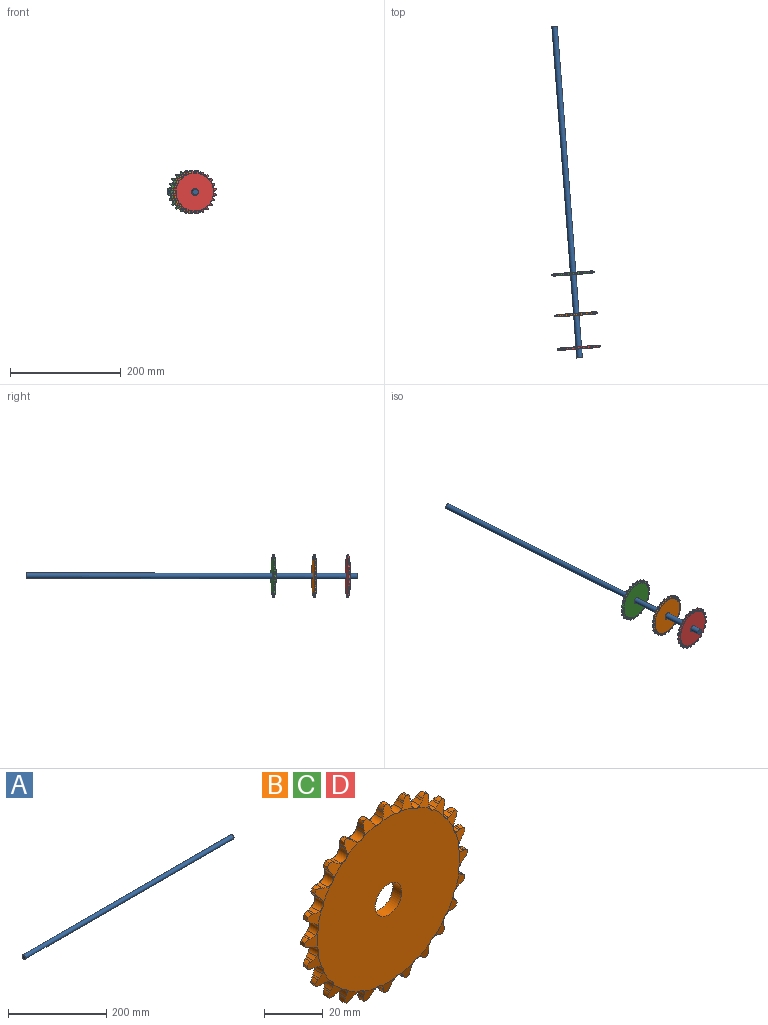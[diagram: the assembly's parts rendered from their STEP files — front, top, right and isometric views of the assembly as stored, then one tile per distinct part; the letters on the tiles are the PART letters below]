
ASSEMBLY  parts=4 mates=3
PART A: 3 faces, bbox 600x10x10 mm
  f0: cylinder r=5mm len=600mm, axis (-1,0,0), area 18849.6mm2, adj f1,f2
  f1: plane 10x10mm, normal (1,0,0), area 78.5mm2, adj f0
  f2: plane 10x10mm, normal (-1,0,0), area 78.5mm2, adj f0
PART B: 243 faces, bbox 78x4.3x78 mm
  f0: cylinder r=38.99mm len=1.91mm, axis (0,1,0), area 2.7mm2, adj f15,f45,f176,f187
  f1: cylinder r=6.35mm len=12.7mm, axis (0,1,0), area 170.3mm2, adj f16,f17
  f2: cylinder r=6.65mm len=3.92mm, axis (0,-1,0), area 6.4mm2, adj f18,f40,f208,f209
  f3: cylinder r=2.59mm len=4.27mm, axis (0,-1,0), area 19.9mm2, adj f16,f17,f20,f21,f42,f43,f196,f197
  f4: cylinder r=2.59mm len=4.27mm, axis (0,-1,0), area 19.9mm2, adj f16,f17,f21,f22,f43,f44,f190,f191
  f5: cylinder r=2.59mm len=4.27mm, axis (0,-1,0), area 19.9mm2, adj f15,f16,f17,f22,f44,f45,f184,f185
  f6: cylinder r=2.59mm len=4.27mm, axis (0,-1,0), area 19.9mm2, adj f15,f16,f17,f23,f45,f46,f178,f179
  f7: cylinder r=2.59mm len=4.27mm, axis (0,-1,0), area 19.9mm2, adj f16,f17,f23,f24,f46,f47,f172,f173
  f8: cylinder r=2.59mm len=4.27mm, axis (0,-1,0), area 19.9mm2, adj f16,f17,f24,f25,f47,f48,f166,f167
  f9: cylinder r=6.65mm len=3.92mm, axis (0,-1,0), area 6.4mm2, adj f27,f50,f154,f155
  f10: cylinder r=4.15mm len=2.78mm, axis (0,-1,0), area 4.8mm2, adj f29,f52,f131,f232
  f11: cylinder r=4.15mm len=2.78mm, axis (0,-1,0), area 4.8mm2, adj f30,f53,f125,f233
  f12: cylinder r=4.15mm len=2.78mm, axis (0,-1,0), area 4.8mm2, adj f38,f60,f82,f241
  f13: cylinder r=4.15mm len=2.78mm, axis (0,-1,0), area 4.8mm2, adj f39,f61,f76,f242
  f14: cone r=34.27mm half-angle=76deg, axis (0,-1,0), area 18.1mm2, adj f16,f97,f98,f99,f100,f107,f108,f109
  f15: cone r=39.03mm half-angle=76deg, axis (0,1,0), area 18.1mm2, adj f0,f5,f6,f17,f176,f177,f178,f185
  f16: plane 68.54x68.54mm, normal (0,1,0), area 3547.1mm2, adj f1,f3,f4,f5,f6,f7,f8,f14
  f17: plane 68.54x68.54mm, normal (0,-1,0), area 3547.1mm2, adj f1,f3,f4,f5,f6,f7,f8,f15
  f18: cone r=39.03mm half-angle=76deg, axis (0,1,0), area 18.2mm2, adj f2,f17,f207,f208,f209,f213,f214,f215
  f19: cone r=39.03mm half-angle=76deg, axis (0,1,0), area 18.1mm2, adj f17,f200,f201,f202,f203,f209,f210,f211
  f20: cone r=39.03mm half-angle=76deg, axis (0,1,0), area 18.1mm2, adj f3,f17,f194,f195,f196,f203,f204,f205
  f21: cone r=39.03mm half-angle=76deg, axis (0,1,0), area 18.1mm2, adj f3,f4,f17,f188,f189,f190,f197,f198
  f22: cone r=39.03mm half-angle=76deg, axis (0,1,0), area 18.1mm2, adj f4,f5,f17,f182,f183,f184,f191,f192
  f23: cone r=39.03mm half-angle=76deg, axis (0,1,0), area 18.1mm2, adj f6,f7,f17,f170,f171,f172,f179,f180
  f24: cone r=39.03mm half-angle=76deg, axis (0,1,0), area 18.1mm2, adj f7,f8,f17,f164,f165,f166,f173,f174
  f25: cone r=39.03mm half-angle=76deg, axis (0,1,0), area 18.1mm2, adj f8,f17,f157,f158,f159,f160,f167,f168
  f26: cone r=39.03mm half-angle=76deg, axis (0,1,0), area 18.1mm2, adj f17,f151,f152,f153,f154,f160,f161,f162
  f27: cone r=39.03mm half-angle=76deg, axis (0,1,0), area 18.2mm2, adj f9,f17,f144,f145,f146,f147,f154,f155
  f28: cone r=39.03mm half-angle=76deg, axis (0,1,0), area 18.1mm2, adj f17,f137,f138,f139,f140,f147,f148,f149
  f29: cone r=39.03mm half-angle=76deg, axis (0,1,0), area 18.2mm2, adj f10,f17,f131,f132,f133,f140,f141,f142
  f30: cone r=39.03mm half-angle=76deg, axis (0,1,0), area 18.2mm2, adj f11,f17,f125,f126,f127,f133,f134,f135
  f31: cone r=39.03mm half-angle=76deg, axis (0,1,0), area 18.1mm2, adj f17,f118,f119,f120,f121,f127,f128,f129
  f32: cone r=39.03mm half-angle=76deg, axis (0,1,0), area 18.1mm2, adj f17,f111,f112,f113,f114,f121,f122,f123
  f33: cone r=39.03mm half-angle=76deg, axis (0,1,0), area 18.1mm2, adj f17,f104,f105,f106,f107,f114,f115,f116
  f34: cone r=39.03mm half-angle=76deg, axis (0,1,0), area 18.1mm2, adj f17,f97,f98,f99,f100,f107,f108,f109
  f35: cone r=39.03mm half-angle=76deg, axis (0,1,0), area 18.1mm2, adj f17,f90,f91,f92,f93,f100,f101,f102
  f36: cone r=39.03mm half-angle=76deg, axis (0,1,0), area 18.1mm2, adj f17,f83,f84,f85,f86,f93,f94,f95
  f37: cone r=39.03mm half-angle=76deg, axis (0,1,0), area 18.1mm2, adj f17,f77,f78,f79,f80,f86,f87,f88
  f38: cone r=39.03mm half-angle=76deg, axis (0,1,0), area 18.2mm2, adj f12,f17,f71,f72,f73,f74,f80,f81
  f39: cone r=39.03mm half-angle=76deg, axis (0,1,0), area 18.2mm2, adj f13,f17,f67,f68,f69,f70,f74,f75
  f40: cone r=34.27mm half-angle=76deg, axis (0,-1,0), area 18.2mm2, adj f2,f16,f207,f208,f209,f213,f214,f215
  f41: cone r=34.27mm half-angle=76deg, axis (0,-1,0), area 18.1mm2, adj f16,f200,f201,f202,f203,f209,f210,f211
  f42: cone r=34.27mm half-angle=76deg, axis (0,-1,0), area 18.1mm2, adj f3,f16,f194,f195,f196,f203,f204,f205
  f43: cone r=34.27mm half-angle=76deg, axis (0,-1,0), area 18.1mm2, adj f3,f4,f16,f188,f189,f190,f197,f198
  f44: cone r=34.27mm half-angle=76deg, axis (0,-1,0), area 18.1mm2, adj f4,f5,f16,f182,f183,f184,f191,f192
  f45: cone r=34.27mm half-angle=76deg, axis (0,-1,0), area 18.1mm2, adj f0,f5,f6,f16,f176,f177,f178,f185
  f46: cone r=34.27mm half-angle=76deg, axis (0,-1,0), area 18.1mm2, adj f6,f7,f16,f170,f171,f172,f179,f180
  f47: cone r=34.27mm half-angle=76deg, axis (0,-1,0), area 18.1mm2, adj f7,f8,f16,f164,f165,f166,f173,f174
  f48: cone r=34.27mm half-angle=76deg, axis (0,-1,0), area 18.1mm2, adj f8,f16,f157,f158,f159,f160,f167,f168
  f49: cone r=34.27mm half-angle=76deg, axis (0,-1,0), area 18.1mm2, adj f16,f151,f152,f153,f154,f160,f161,f162
  f50: cone r=34.27mm half-angle=76deg, axis (0,-1,0), area 18.2mm2, adj f9,f16,f144,f145,f146,f147,f154,f155
  f51: cone r=34.27mm half-angle=76deg, axis (0,-1,0), area 18.1mm2, adj f16,f137,f138,f139,f140,f147,f148,f149
  f52: cone r=34.27mm half-angle=76deg, axis (0,-1,0), area 18.2mm2, adj f10,f16,f131,f132,f133,f140,f141,f142
  f53: cone r=34.27mm half-angle=76deg, axis (0,-1,0), area 18.2mm2, adj f11,f16,f125,f126,f127,f133,f134,f135
  f54: cone r=34.27mm half-angle=76deg, axis (0,-1,0), area 18.1mm2, adj f16,f118,f119,f120,f121,f127,f128,f129
  f55: cone r=34.27mm half-angle=76deg, axis (0,-1,0), area 18.1mm2, adj f16,f111,f112,f113,f114,f121,f122,f123
  f56: cone r=34.27mm half-angle=76deg, axis (0,-1,0), area 18.1mm2, adj f16,f104,f105,f106,f107,f114,f115,f116
  f57: cone r=34.27mm half-angle=76deg, axis (0,-1,0), area 18.1mm2, adj f16,f90,f91,f92,f93,f100,f101,f102
  f58: cone r=34.27mm half-angle=76deg, axis (0,-1,0), area 18.1mm2, adj f16,f83,f84,f85,f86,f93,f94,f95
  f59: cone r=34.27mm half-angle=76deg, axis (0,-1,0), area 18.1mm2, adj f16,f77,f78,f79,f80,f86,f87,f88
  f60: cone r=34.27mm half-angle=76deg, axis (0,-1,0), area 18.2mm2, adj f12,f16,f71,f72,f73,f74,f80,f81
  f61: cone r=34.27mm half-angle=76deg, axis (0,-1,0), area 18.2mm2, adj f13,f16,f67,f68,f69,f70,f74,f75
  f62: cone r=39.03mm half-angle=76deg, axis (0,1,0), area 18.1mm2, adj f17,f64,f65,f66,f67,f216,f217,f218
  f63: cone r=34.27mm half-angle=76deg, axis (0,-1,0), area 18.1mm2, adj f16,f64,f65,f66,f67,f216,f217,f218
  f64: cylinder r=4.15mm len=2.78mm, axis (0,-1,0), area 4.8mm2, adj f62,f63,f65,f220
  f65: plane 3.1x0.64mm, normal (0.97,0,-0.25), area 2mm2, adj f62,f63,f64,f66
  f66: cylinder r=6.65mm len=3.92mm, axis (0,-1,0), area 6.4mm2, adj f62,f63,f65,f67
  f67: cylinder r=2.59mm len=4.27mm, axis (0,-1,0), area 19.9mm2, adj f16,f17,f39,f61,f62,f63,f66,f68
  f68: cylinder r=6.65mm len=3.92mm, axis (0,-1,0), area 6.4mm2, adj f39,f61,f67,f69
  f69: plane 3.1x0.58mm, normal (-0.87,0,-0.49), area 2mm2, adj f39,f61,f68,f70
  f70: cylinder r=4.15mm len=2.78mm, axis (0,-1,0), area 4.8mm2, adj f39,f61,f69,f242
  f71: cylinder r=4.15mm len=2.78mm, axis (0,-1,0), area 4.8mm2, adj f38,f60,f72,f241
  f72: plane 3.1x0.48mm, normal (-0.72,0,-0.7), area 2mm2, adj f38,f60,f71,f73
  f73: cylinder r=6.65mm len=3.92mm, axis (0,-1,0), area 6.4mm2, adj f38,f60,f72,f74
  f74: cylinder r=2.59mm len=4.27mm, axis (0,-1,0), area 19.9mm2, adj f16,f17,f38,f39,f60,f61,f73,f75
  f75: cylinder r=6.65mm len=3.92mm, axis (0,-1,0), area 6.4mm2, adj f39,f61,f74,f76
  f76: plane 3.1x0.66mm, normal (1,0,0.01), area 2mm2, adj f13,f39,f61,f75
  f77: cylinder r=4.15mm len=2.78mm, axis (0,-1,0), area 4.8mm2, adj f37,f59,f78,f240
  f78: plane 3.1x0.57mm, normal (-0.51,0,-0.86), area 2mm2, adj f37,f59,f77,f79
  f79: cylinder r=6.65mm len=3.92mm, axis (0,-1,0), area 6.4mm2, adj f37,f59,f78,f80
  f80: cylinder r=2.59mm len=4.27mm, axis (0,-1,0), area 19.9mm2, adj f16,f17,f37,f38,f59,f60,f79,f81
  f81: cylinder r=6.65mm len=3.92mm, axis (0,-1,0), area 6.4mm2, adj f38,f60,f80,f82
  f82: plane 3.1x0.64mm, normal (0.96,0,0.27), area 2mm2, adj f12,f38,f60,f81
  f83: cylinder r=4.15mm len=2.78mm, axis (0,-1,0), area 4.8mm2, adj f36,f58,f84,f239
  f84: plane 3.1x0.64mm, normal (-0.27,0,-0.96), area 2mm2, adj f36,f58,f83,f85
  f85: cylinder r=6.65mm len=3.92mm, axis (0,-1,0), area 6.4mm2, adj f36,f58,f84,f86
  f86: cylinder r=2.59mm len=4.27mm, axis (0,-1,0), area 19.9mm2, adj f16,f17,f36,f37,f58,f59,f85,f87
  f87: cylinder r=6.65mm len=3.92mm, axis (0,-1,0), area 6.4mm2, adj f37,f59,f86,f88
  f88: plane 3.1x0.57mm, normal (0.86,0,0.51), area 2mm2, adj f37,f59,f87,f89
  f89: cylinder r=4.15mm len=2.78mm, axis (0,-1,0), area 4.8mm2, adj f37,f59,f88,f240
  f90: cylinder r=4.15mm len=2.78mm, axis (0,-1,0), area 4.8mm2, adj f35,f57,f91,f238
  f91: plane 3.1x0.66mm, normal (-0.01,0,-1), area 2mm2, adj f35,f57,f90,f92
  f92: cylinder r=6.65mm len=3.92mm, axis (0,-1,0), area 6.4mm2, adj f35,f57,f91,f93
  f93: cylinder r=2.59mm len=4.27mm, axis (0,-1,0), area 19.9mm2, adj f16,f17,f35,f36,f57,f58,f92,f94
  f94: cylinder r=6.65mm len=3.92mm, axis (0,-1,0), area 6.4mm2, adj f36,f58,f93,f95
  f95: plane 3.1x0.48mm, normal (0.7,0,0.72), area 2mm2, adj f36,f58,f94,f96
  f96: cylinder r=4.15mm len=2.78mm, axis (0,-1,0), area 4.8mm2, adj f36,f58,f95,f239
  f97: cylinder r=4.15mm len=2.78mm, axis (0,-1,0), area 4.8mm2, adj f14,f34,f98,f237
  f98: plane 3.1x0.64mm, normal (0.25,0,-0.97), area 2mm2, adj f14,f34,f97,f99
  f99: cylinder r=6.65mm len=3.92mm, axis (0,-1,0), area 6.4mm2, adj f14,f34,f98,f100
  f100: cylinder r=2.59mm len=4.27mm, axis (0,-1,0), area 19.9mm2, adj f14,f16,f17,f34,f35,f57,f99,f101
  f101: cylinder r=6.65mm len=3.92mm, axis (0,-1,0), area 6.4mm2, adj f35,f57,f100,f102
  f102: plane 3.1x0.58mm, normal (0.49,0,0.87), area 2mm2, adj f35,f57,f101,f103
  f103: cylinder r=4.15mm len=2.78mm, axis (0,-1,0), area 4.8mm2, adj f35,f57,f102,f238
  f104: cylinder r=4.15mm len=2.78mm, axis (0,-1,0), area 4.8mm2, adj f33,f56,f105,f236
  f105: plane 3.1x0.58mm, normal (0.49,0,-0.87), area 2mm2, adj f33,f56,f104,f106
  f106: cylinder r=6.65mm len=3.92mm, axis (0,-1,0), area 6.4mm2, adj f33,f56,f105,f107
  f107: cylinder r=2.59mm len=4.27mm, axis (0,-1,0), area 19.9mm2, adj f14,f16,f17,f33,f34,f56,f106,f108
  f108: cylinder r=6.65mm len=3.92mm, axis (0,-1,0), area 6.4mm2, adj f14,f34,f107,f109
  f109: plane 3.1x0.64mm, normal (0.25,0,0.97), area 2mm2, adj f14,f34,f108,f110
  f110: cylinder r=4.15mm len=2.78mm, axis (0,-1,0), area 4.8mm2, adj f14,f34,f109,f237
  f111: cylinder r=4.15mm len=2.78mm, axis (0,-1,0), area 4.8mm2, adj f32,f55,f112,f235
  f112: plane 3.1x0.48mm, normal (0.7,0,-0.72), area 2mm2, adj f32,f55,f111,f113
  f113: cylinder r=6.65mm len=3.92mm, axis (0,-1,0), area 6.4mm2, adj f32,f55,f112,f114
  f114: cylinder r=2.59mm len=4.27mm, axis (0,-1,0), area 19.9mm2, adj f16,f17,f32,f33,f55,f56,f113,f115
  f115: cylinder r=6.65mm len=3.92mm, axis (0,-1,0), area 6.4mm2, adj f33,f56,f114,f116
  f116: plane 3.1x0.66mm, normal (-0.01,0,1), area 2mm2, adj f33,f56,f115,f117
  f117: cylinder r=4.15mm len=2.78mm, axis (0,-1,0), area 4.8mm2, adj f33,f56,f116,f236
  f118: cylinder r=4.15mm len=2.78mm, axis (0,-1,0), area 4.8mm2, adj f31,f54,f119,f234
  f119: plane 3.1x0.57mm, normal (0.86,0,-0.51), area 2mm2, adj f31,f54,f118,f120
  f120: cylinder r=6.65mm len=3.92mm, axis (0,-1,0), area 6.4mm2, adj f31,f54,f119,f121
  f121: cylinder r=2.59mm len=4.27mm, axis (0,-1,0), area 19.9mm2, adj f16,f17,f31,f32,f54,f55,f120,f122
  f122: cylinder r=6.65mm len=3.92mm, axis (0,-1,0), area 6.4mm2, adj f32,f55,f121,f123
  f123: plane 3.1x0.64mm, normal (-0.27,0,0.96), area 2mm2, adj f32,f55,f122,f124
  f124: cylinder r=4.15mm len=2.78mm, axis (0,-1,0), area 4.8mm2, adj f32,f55,f123,f235
  f125: plane 3.1x0.64mm, normal (0.96,0,-0.27), area 2mm2, adj f11,f30,f53,f126
  f126: cylinder r=6.65mm len=3.92mm, axis (0,-1,0), area 6.4mm2, adj f30,f53,f125,f127
  f127: cylinder r=2.59mm len=4.27mm, axis (0,-1,0), area 19.9mm2, adj f16,f17,f30,f31,f53,f54,f126,f128
  f128: cylinder r=6.65mm len=3.92mm, axis (0,-1,0), area 6.4mm2, adj f31,f54,f127,f129
  f129: plane 3.1x0.57mm, normal (-0.51,0,0.86), area 2mm2, adj f31,f54,f128,f130
  f130: cylinder r=4.15mm len=2.78mm, axis (0,-1,0), area 4.8mm2, adj f31,f54,f129,f234
  f131: plane 3.1x0.66mm, normal (1,0,-0.01), area 2mm2, adj f10,f29,f52,f132
  f132: cylinder r=6.65mm len=3.92mm, axis (0,-1,0), area 6.4mm2, adj f29,f52,f131,f133
  f133: cylinder r=2.59mm len=4.27mm, axis (0,-1,0), area 19.9mm2, adj f16,f17,f29,f30,f52,f53,f132,f134
  f134: cylinder r=6.65mm len=3.92mm, axis (0,-1,0), area 6.4mm2, adj f30,f53,f133,f135
  f135: plane 3.1x0.48mm, normal (-0.72,0,0.7), area 2mm2, adj f30,f53,f134,f136
  f136: cylinder r=4.15mm len=2.78mm, axis (0,-1,0), area 4.8mm2, adj f30,f53,f135,f233
  f137: cylinder r=4.15mm len=2.78mm, axis (0,-1,0), area 4.8mm2, adj f28,f51,f138,f231
  f138: plane 3.1x0.64mm, normal (0.97,0,0.25), area 2mm2, adj f28,f51,f137,f139
  f139: cylinder r=6.65mm len=3.92mm, axis (0,-1,0), area 6.4mm2, adj f28,f51,f138,f140
  f140: cylinder r=2.59mm len=4.27mm, axis (0,-1,0), area 19.9mm2, adj f16,f17,f28,f29,f51,f52,f139,f141
  f141: cylinder r=6.65mm len=3.92mm, axis (0,-1,0), area 6.4mm2, adj f29,f52,f140,f142
  f142: plane 3.1x0.58mm, normal (-0.87,0,0.49), area 2mm2, adj f29,f52,f141,f143
  f143: cylinder r=4.15mm len=2.78mm, axis (0,-1,0), area 4.8mm2, adj f29,f52,f142,f232
  f144: cylinder r=4.15mm len=2.78mm, axis (0,-1,0), area 4.8mm2, adj f27,f50,f145,f230
  f145: plane 3.1x0.58mm, normal (0.87,0,0.49), area 2mm2, adj f27,f50,f144,f146
  f146: cylinder r=6.65mm len=3.92mm, axis (0,-1,0), area 6.4mm2, adj f27,f50,f145,f147
  f147: cylinder r=2.59mm len=4.27mm, axis (0,-1,0), area 19.9mm2, adj f16,f17,f27,f28,f50,f51,f146,f148
  f148: cylinder r=6.65mm len=3.92mm, axis (0,-1,0), area 6.4mm2, adj f28,f51,f147,f149
  f149: plane 3.1x0.64mm, normal (-0.97,0,0.25), area 2mm2, adj f28,f51,f148,f150
  f150: cylinder r=4.15mm len=2.78mm, axis (0,-1,0), area 4.8mm2, adj f28,f51,f149,f231
  f151: cylinder r=4.15mm len=2.78mm, axis (0,-1,0), area 4.8mm2, adj f26,f49,f152,f229
  f152: plane 3.1x0.48mm, normal (0.72,0,0.7), area 2mm2, adj f26,f49,f151,f153
  f153: cylinder r=6.65mm len=3.92mm, axis (0,-1,0), area 6.4mm2, adj f26,f49,f152,f154
  f154: cylinder r=2.59mm len=4.27mm, axis (0,-1,0), area 19.9mm2, adj f9,f16,f17,f26,f27,f49,f50,f153
  f155: plane 3.1x0.66mm, normal (-1,0,-0.01), area 2mm2, adj f9,f27,f50,f156
  f156: cylinder r=4.15mm len=2.78mm, axis (0,-1,0), area 4.8mm2, adj f27,f50,f155,f230
  f157: cylinder r=4.15mm len=2.78mm, axis (0,-1,0), area 4.8mm2, adj f25,f48,f158,f228
  f158: plane 3.1x0.57mm, normal (0.51,0,0.86), area 2mm2, adj f25,f48,f157,f159
  f159: cylinder r=6.65mm len=3.92mm, axis (0,-1,0), area 6.4mm2, adj f25,f48,f158,f160
  f160: cylinder r=2.59mm len=4.27mm, axis (0,-1,0), area 19.9mm2, adj f16,f17,f25,f26,f48,f49,f159,f161
  f161: cylinder r=6.65mm len=3.92mm, axis (0,-1,0), area 6.4mm2, adj f26,f49,f160,f162
  f162: plane 3.1x0.64mm, normal (-0.96,0,-0.27), area 2mm2, adj f26,f49,f161,f163
  f163: cylinder r=4.15mm len=2.78mm, axis (0,-1,0), area 4.8mm2, adj f26,f49,f162,f229
  f164: cylinder r=4.15mm len=2.78mm, axis (0,-1,0), area 4.8mm2, adj f24,f47,f165,f227
  f165: plane 3.1x0.64mm, normal (0.27,0,0.96), area 2mm2, adj f24,f47,f164,f166
  f166: cylinder r=6.65mm len=3.92mm, axis (0,-1,0), area 6.4mm2, adj f8,f24,f47,f165
  f167: cylinder r=6.65mm len=3.92mm, axis (0,-1,0), area 6.4mm2, adj f8,f25,f48,f168
  f168: plane 3.1x0.57mm, normal (-0.86,0,-0.51), area 2mm2, adj f25,f48,f167,f169
  f169: cylinder r=4.15mm len=2.78mm, axis (0,-1,0), area 4.8mm2, adj f25,f48,f168,f228
  f170: cylinder r=4.15mm len=2.78mm, axis (0,-1,0), area 4.8mm2, adj f23,f46,f171,f226
  f171: plane 3.1x0.66mm, normal (0.01,0,1), area 2mm2, adj f23,f46,f170,f172
  f172: cylinder r=6.65mm len=3.92mm, axis (0,-1,0), area 6.4mm2, adj f7,f23,f46,f171
  f173: cylinder r=6.65mm len=3.92mm, axis (0,-1,0), area 6.4mm2, adj f7,f24,f47,f174
  f174: plane 3.1x0.48mm, normal (-0.7,0,-0.72), area 2mm2, adj f24,f47,f173,f175
  f175: cylinder r=4.15mm len=2.78mm, axis (0,-1,0), area 4.8mm2, adj f24,f47,f174,f227
  f176: cylinder r=4.15mm len=2.78mm, axis (0,-1,0), area 4.8mm2, adj f0,f15,f45,f177
  f177: plane 3.1x0.64mm, normal (-0.25,0,0.97), area 2mm2, adj f15,f45,f176,f178
  f178: cylinder r=6.65mm len=3.92mm, axis (0,-1,0), area 6.4mm2, adj f6,f15,f45,f177
  f179: cylinder r=6.65mm len=3.92mm, axis (0,-1,0), area 6.4mm2, adj f6,f23,f46,f180
  f180: plane 3.1x0.58mm, normal (-0.49,0,-0.87), area 2mm2, adj f23,f46,f179,f181
  f181: cylinder r=4.15mm len=2.78mm, axis (0,-1,0), area 4.8mm2, adj f23,f46,f180,f226
  f182: cylinder r=4.15mm len=2.78mm, axis (0,-1,0), area 4.8mm2, adj f22,f44,f183,f225
  f183: plane 3.1x0.58mm, normal (-0.49,0,0.87), area 2mm2, adj f22,f44,f182,f184
  f184: cylinder r=6.65mm len=3.92mm, axis (0,-1,0), area 6.4mm2, adj f5,f22,f44,f183
  f185: cylinder r=6.65mm len=3.92mm, axis (0,-1,0), area 6.4mm2, adj f5,f15,f45,f186
  f186: plane 3.1x0.64mm, normal (-0.25,0,-0.97), area 2mm2, adj f15,f45,f185,f187
  f187: cylinder r=4.15mm len=2.78mm, axis (0,-1,0), area 4.8mm2, adj f0,f15,f45,f186
  f188: cylinder r=4.15mm len=2.78mm, axis (0,-1,0), area 4.8mm2, adj f21,f43,f189,f224
  f189: plane 3.1x0.48mm, normal (-0.7,0,0.72), area 2mm2, adj f21,f43,f188,f190
  f190: cylinder r=6.65mm len=3.92mm, axis (0,-1,0), area 6.4mm2, adj f4,f21,f43,f189
  f191: cylinder r=6.65mm len=3.92mm, axis (0,-1,0), area 6.4mm2, adj f4,f22,f44,f192
  f192: plane 3.1x0.66mm, normal (0.01,0,-1), area 2mm2, adj f22,f44,f191,f193
  f193: cylinder r=4.15mm len=2.78mm, axis (0,-1,0), area 4.8mm2, adj f22,f44,f192,f225
  f194: cylinder r=4.15mm len=2.78mm, axis (0,-1,0), area 4.8mm2, adj f20,f42,f195,f223
  f195: plane 3.1x0.57mm, normal (-0.86,0,0.51), area 2mm2, adj f20,f42,f194,f196
  f196: cylinder r=6.65mm len=3.92mm, axis (0,-1,0), area 6.4mm2, adj f3,f20,f42,f195
  f197: cylinder r=6.65mm len=3.92mm, axis (0,-1,0), area 6.4mm2, adj f3,f21,f43,f198
  f198: plane 3.1x0.64mm, normal (0.27,0,-0.96), area 2mm2, adj f21,f43,f197,f199
  f199: cylinder r=4.15mm len=2.78mm, axis (0,-1,0), area 4.8mm2, adj f21,f43,f198,f224
  f200: cylinder r=4.15mm len=2.78mm, axis (0,-1,0), area 4.8mm2, adj f19,f41,f201,f222
  f201: plane 3.1x0.64mm, normal (-0.96,0,0.27), area 2mm2, adj f19,f41,f200,f202
  f202: cylinder r=6.65mm len=3.92mm, axis (0,-1,0), area 6.4mm2, adj f19,f41,f201,f203
  f203: cylinder r=2.59mm len=4.27mm, axis (0,-1,0), area 19.9mm2, adj f16,f17,f19,f20,f41,f42,f202,f204
  f204: cylinder r=6.65mm len=3.92mm, axis (0,-1,0), area 6.4mm2, adj f20,f42,f203,f205
  f205: plane 3.1x0.57mm, normal (0.51,0,-0.86), area 2mm2, adj f20,f42,f204,f206
  f206: cylinder r=4.15mm len=2.78mm, axis (0,-1,0), area 4.8mm2, adj f20,f42,f205,f223
  f207: cylinder r=4.15mm len=2.78mm, axis (0,-1,0), area 4.8mm2, adj f18,f40,f208,f221
  f208: plane 3.1x0.66mm, normal (-1,0,0.01), area 2mm2, adj f2,f18,f40,f207
  f209: cylinder r=2.59mm len=4.27mm, axis (0,-1,0), area 19.9mm2, adj f2,f16,f17,f18,f19,f40,f41,f210
  f210: cylinder r=6.65mm len=3.92mm, axis (0,-1,0), area 6.4mm2, adj f19,f41,f209,f211
  f211: plane 3.1x0.48mm, normal (0.72,0,-0.7), area 2mm2, adj f19,f41,f210,f212
  f212: cylinder r=4.15mm len=2.78mm, axis (0,-1,0), area 4.8mm2, adj f19,f41,f211,f222
  f213: cylinder r=4.15mm len=2.78mm, axis (0,-1,0), area 4.8mm2, adj f18,f40,f214,f221
  f214: plane 3.1x0.58mm, normal (0.87,0,-0.49), area 2mm2, adj f18,f40,f213,f215
  f215: cylinder r=6.65mm len=3.92mm, axis (0,-1,0), area 6.4mm2, adj f18,f40,f214,f216
  f216: cylinder r=2.59mm len=4.27mm, axis (0,-1,0), area 19.9mm2, adj f16,f17,f18,f40,f62,f63,f215,f217
  f217: cylinder r=6.65mm len=3.92mm, axis (0,-1,0), area 6.4mm2, adj f62,f63,f216,f218
  f218: plane 3.1x0.64mm, normal (-0.97,0,-0.25), area 2mm2, adj f62,f63,f217,f219
  f219: cylinder r=4.15mm len=2.78mm, axis (0,-1,0), area 4.8mm2, adj f62,f63,f218,f220
  f220: cylinder r=38.99mm len=1.91mm, axis (0,1,0), area 2.7mm2, adj f62,f63,f64,f219
  f221: cylinder r=38.99mm len=1.91mm, axis (0,1,0), area 2.7mm2, adj f18,f40,f207,f213
  f222: cylinder r=38.99mm len=1.91mm, axis (0,1,0), area 2.7mm2, adj f19,f41,f200,f212
  f223: cylinder r=38.99mm len=1.91mm, axis (0,1,0), area 2.7mm2, adj f20,f42,f194,f206
  f224: cylinder r=38.99mm len=1.91mm, axis (0,1,0), area 2.7mm2, adj f21,f43,f188,f199
  f225: cylinder r=38.99mm len=1.91mm, axis (0,1,0), area 2.7mm2, adj f22,f44,f182,f193
  f226: cylinder r=38.99mm len=1.91mm, axis (0,1,0), area 2.7mm2, adj f23,f46,f170,f181
  f227: cylinder r=38.99mm len=1.91mm, axis (0,1,0), area 2.7mm2, adj f24,f47,f164,f175
  f228: cylinder r=38.99mm len=1.91mm, axis (0,1,0), area 2.7mm2, adj f25,f48,f157,f169
  f229: cylinder r=38.99mm len=1.91mm, axis (0,1,0), area 2.7mm2, adj f26,f49,f151,f163
  f230: cylinder r=38.99mm len=1.91mm, axis (0,1,0), area 2.7mm2, adj f27,f50,f144,f156
  f231: cylinder r=38.99mm len=1.91mm, axis (0,1,0), area 2.7mm2, adj f28,f51,f137,f150
  f232: cylinder r=38.99mm len=1.91mm, axis (0,1,0), area 2.7mm2, adj f10,f29,f52,f143
  f233: cylinder r=38.99mm len=1.91mm, axis (0,1,0), area 2.7mm2, adj f11,f30,f53,f136
  f234: cylinder r=38.99mm len=1.91mm, axis (0,1,0), area 2.7mm2, adj f31,f54,f118,f130
  f235: cylinder r=38.99mm len=1.91mm, axis (0,1,0), area 2.7mm2, adj f32,f55,f111,f124
  f236: cylinder r=38.99mm len=1.91mm, axis (0,1,0), area 2.7mm2, adj f33,f56,f104,f117
  f237: cylinder r=38.99mm len=1.91mm, axis (0,1,0), area 2.7mm2, adj f14,f34,f97,f110
  f238: cylinder r=38.99mm len=1.91mm, axis (0,1,0), area 2.7mm2, adj f35,f57,f90,f103
  f239: cylinder r=38.99mm len=1.91mm, axis (0,1,0), area 2.7mm2, adj f36,f58,f83,f96
  f240: cylinder r=38.99mm len=1.91mm, axis (0,1,0), area 2.7mm2, adj f37,f59,f77,f89
  f241: cylinder r=38.99mm len=1.91mm, axis (0,1,0), area 2.7mm2, adj f12,f38,f60,f71
  f242: cylinder r=38.99mm len=1.91mm, axis (0,1,0), area 2.7mm2, adj f13,f39,f61,f70
PART C: same geometry as B
PART D: same geometry as B
PLACE A rot(axis=(0.38,0.41,0.83),105deg) t=(-479.91,5.28,235.54)mm
PLACE B rot(axis=(0.04,-0.99,0.11),37.3deg) t=(-54.43,116.61,-6.41)mm
PLACE C rot(axis=(0.04,-0.99,0.11),37.3deg) t=(-59.98,190.24,-6.3)mm
PLACE D rot(axis=(0.04,-0.99,0.11),37.3deg) t=(-49.87,56.16,-6.5)mm
MATE slider A.f0 <-> C.f0  axis (-0.08,1,0) through (-48.52,38.16,-6.52)mm
MATE slider A.f0 <-> D.f0  axis (-0.08,1,0) through (-48.52,38.16,-6.52)mm
MATE slider A.f0 <-> B.f0  axis (0.08,-1,0) through (-48.52,38.16,-6.52)mm
